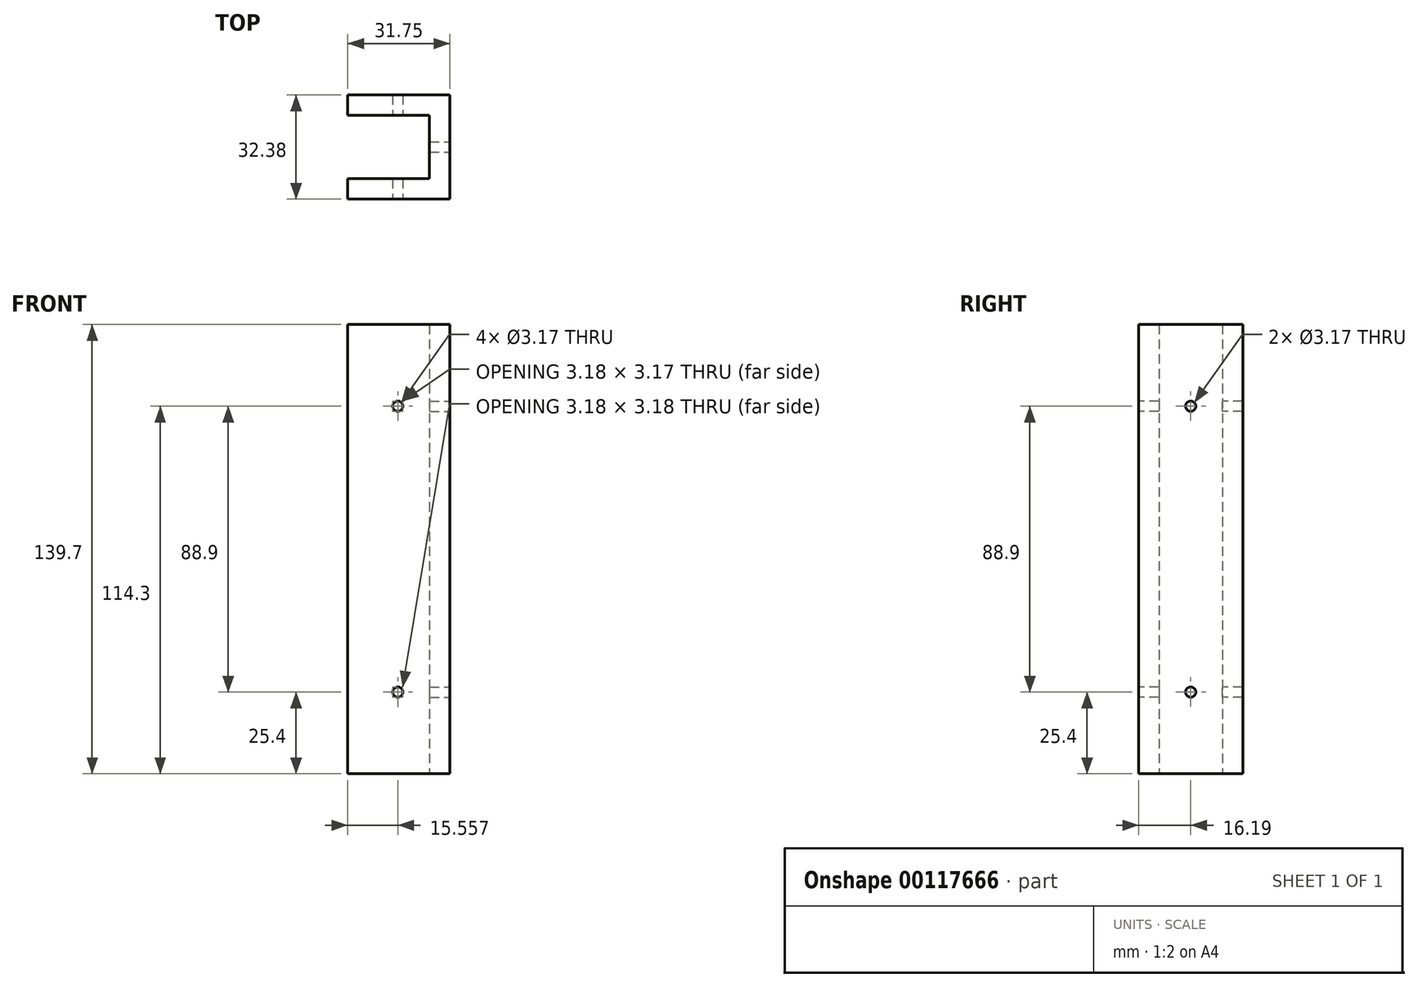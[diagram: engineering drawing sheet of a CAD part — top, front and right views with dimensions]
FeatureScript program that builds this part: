
annotation { "Feature Type Name" : "Feature", "Feature Type Description" : "" }
export const myFeature = defineFeature(function(context is Context, id is Id, definition is map)
    precondition{}
    {
        {
            var Q0;
            Q0=qCreatedBy(makeId("Top.planeOp"),FACE);
            var sketch = newSketch(context, id + "F0", { "sketchPlane" : qUnion([Q0])});
            skLineSegment(sketch, "E0", {"start": v(-12.7, -9.84) * mm, "end": v(12.7, -9.84) * mm});
            skLineSegment(sketch, "E1", {"start": v(12.7, -9.84) * mm, "end": v(12.7, 9.84) * mm});
            skLineSegment(sketch, "E2", {"start": v(12.7, 9.84) * mm, "end": v(-12.7, 9.84) * mm});
            skLineSegment(sketch, "E3", {"start": v(-12.7, 9.84) * mm, "end": v(-12.7, 16.2) * mm});
            skLineSegment(sketch, "E4", {"start": v(-12.7, 16.2) * mm, "end": v(19.05, 16.2) * mm});
            skLineSegment(sketch, "E5", {"start": v(19.05, 16.2) * mm, "end": v(19.05, -16.2) * mm});
            skLineSegment(sketch, "E6", {"start": v(19.05, -16.2) * mm, "end": v(-12.7, -16.2) * mm});
            skLineSegment(sketch, "E7", {"start": v(-12.7, -16.2) * mm, "end": v(-12.7, -9.84) * mm});
            skSolve(sketch);
        }
        {
            var Q0;
            Q0 = qSketchRegion(id + "F0", true);
            extrude(context, id + "F1", {"entities" : qUnion([Q0]), "depth" : 139.7 * mm});
        }
        {
            var Q0;
            Q0=makeQuery(id+"F1.opExtrude","SWEPT_FACE",FACE,{"disambiguationData":[OSD([sQuery(id+"F0.wireOp",EDGE,"E5")])]});
            var sketch = newSketch(context, id + "F2", { "sketchPlane" : qUnion([Q0])});
            skCircle(sketch, "E8", {"center": v(0, 114.3) * mm, "radius": 1.59 * mm});
            skCircle(sketch, "E9", {"center": v(0, 25.4) * mm, "radius": 1.59 * mm});
            skSolve(sketch);
        }
        {
            var Q0;
            Q0 = qSketchRegion(id + "F2", true);
            extrude(context, id + "F3", {"entities" : qUnion([Q0]), "operationType" : NewBodyOperationType.REMOVE, "endBound" : BoundingType.THROUGH_ALL, "oppositeDirection" : true, "depth" : 25.4 * mm});
        }
        {
            var Q0;
            Q0=makeQuery(id+"F1.opExtrude","SWEPT_FACE",FACE,{"disambiguationData":[OSD([sQuery(id+"F0.wireOp",EDGE,"E6")])]});
            var sketch = newSketch(context, id + "F4", { "sketchPlane" : qUnion([Q0])});
            skCircle(sketch, "E10", {"center": v(2.86, 114.3) * mm, "radius": 1.59 * mm});
            skCircle(sketch, "E11", {"center": v(2.86, 25.4) * mm, "radius": 1.59 * mm});
            skSolve(sketch);
        }
        {
            var Q0;
            Q0 = qSketchRegion(id + "F4", true);
            extrude(context, id + "F5", {"entities" : qUnion([Q0]), "operationType" : NewBodyOperationType.REMOVE, "endBound" : BoundingType.THROUGH_ALL, "oppositeDirection" : true, "depth" : 25.4 * mm});
        }
    });
